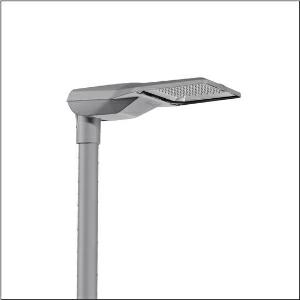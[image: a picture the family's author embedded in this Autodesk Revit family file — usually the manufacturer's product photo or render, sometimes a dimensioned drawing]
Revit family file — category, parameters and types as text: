
# Revit family: streetlight_sl_21_iq_midi___st0_5a_5xe3b31d08nb_970f
name_source: partatom
category: Lighting Fixtures
units: mm (PartAtom-declared; Revit-internal decimal feet)

## family parameters
Cut with Voids When Loaded = No
Host = Face
Light Source = No
Part Type = Normal
Room Calculation Point = No
Round Connector Dimension = Use Diameter
Shared = No

## types (1)
- --- (1 x LED, 23230 lm, 155.5 W, 3000K)
    Apparent Load = 155 VA
    CIE Flux Codes = 43 76 97 100 100
    Color Rendering = 70
    Color Temperature = 3000K
    Default Elevation = 1800 mm
    Description = Streetlight SL 21 iQ midi, mast luminaire, primary light control with lens, of PMMA, primary optical cover: cover, of toughened safety glass, transparent, light distribution: ST0.5a, light emission: direct distribution, primary light characteristic: asymmetric, installation type: post-top, side-entry, LED, High Power LED, rated luminous flux: 23.230lm, luminous efficacy: 149lm/W, light colour: 730, colour temperature: 3000K, control: Auto-Match, Temp-Guard, Lumen-Switch, Night-Set, Smart-Wire, Light-Fading, Desk-Remote (wireless, voltage-free reading and setting of iQ features in the workshop via application-optimized NFC function/RFID function), optimised constant luminous flux control (CLO 2.0), pre-setting: linear dimming characteristic, mains connection: 230..240V, AC, 50/60Hz, start of lifetime: 156W, end of service life: 162W, reduction: 69W, luminaire housing, of diecast aluminium, powder-coated, Siteco® metallic grey (DB 702S), corrosivity category C5 mid according to DIN EN ISO 12944, please order mast flange separately, inclination adjustable: 0°, 5°, 10°, 15°, sealing non-destructively replaceable, multi-level sealing system, length: 644mm, width: 335mm, height: 110mm, mast flange for spigot size: 42mm (side-entry): 5XC10008XM4, 60/48mm (side-entry/post-top): 5XC10108XM2, 76/60mm (side-entry/post-top): 5XC10108XM1, protection rating (complete): IP66, insulation class (complete): insulation class II (safety insulation), certification: CE, ENEC, ENEC+, VDE, impact resistance: IK09, permissible operating ambient temperature for outdoor applications: -40..+50°C, standard-compliant lighting for roads and squares, packaging unit: 1 piece

Light Distribution: ST0.5a
    Height = 111 mm
    Lamp = 1 x LED
    Lamp Light Flux = 23230 lm
    Lamp Power = 155.5 W
    Lamp count = 1
    Length = 644 mm
    Luminous efficacy = 149 lm/W
    Manufacturer = Siteco
    ModVariant = No
    Model = 5XE3B31D08NB
    Number of Poles = 1
    OnlyDefault = Yes
    Power Factor = 1
    Product Name = Streetlight SL 21 iQ midi | ST0.5a
    Product group = mast luminaire | pylon top
    ProductGroupID = 6100
    Protection Class = Protection class II
    Protection Degree = IP 66
    RLX_Detail_Level = 1
    RLX_Emergency_Light_Flux = 0 lm
    RLX_Emergency_Type = 0
    RLX_Emergency_Type_DB = No
    RlxData = <blob elided: 102137 chars, md5=5cb9c4c2>
    Socket = socket
    Standby Power = 0 W
    System Light Flux = 23230 lm
    System Power = 155 W
    Type Comments = factory setting: luminous flux: 100 % | dim-lin: 254 | 823 mA
    Type Image = l_1004298.jpg
    URL = http://relux.com
    VarID = @adj_142543
    Voltage = 0 V
    Weight = 0.00 kg
    Width = 336 mm

## geometry (parser evidence)
native form markers: Blend x4, Sweep x10
no freeform markers — native parametric forms only
